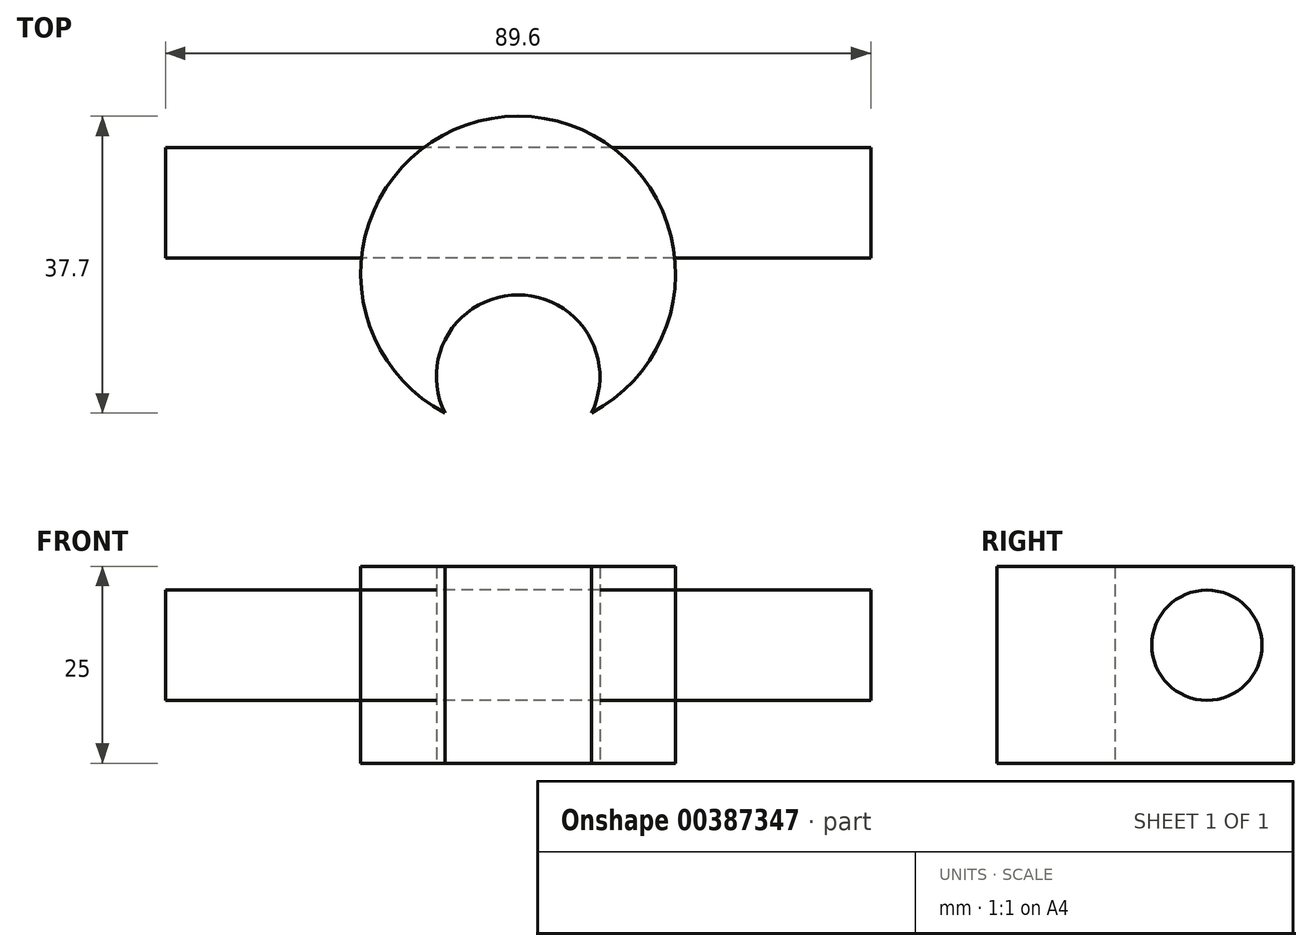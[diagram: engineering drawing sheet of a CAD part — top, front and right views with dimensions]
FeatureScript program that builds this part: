
annotation { "Feature Type Name" : "Feature", "Feature Type Description" : "" }
export const myFeature = defineFeature(function(context is Context, id is Id, definition is map)
    precondition{}
    {
        {
            var Q0;
            Q0=qCreatedBy(makeId("Top.planeOp"),FACE);
            var sketch = newSketch(context, id + "F0", { "sketchPlane" : qUnion([Q0])});
            skCircle(sketch, "E0", {"center": v(0, 0) * mm, "radius": 20 * mm});
            skCircle(sketch, "E1", {"center": v(0, -13.1) * mm, "radius": 10.39 * mm});
            skLineSegment(sketch, "E2", {"start": v(0, 20) * mm, "end": v(0, 20) * mm});
            skSolve(sketch);
        }
        {
            var Q0;
            {var subQ0=sQuery(id+"F0.wireOp",EDGE,"E1");var subQ1=sQuery(id+"F0.wireOp",EDGE,"E0");var subQ2=makeQuery(id+"F0.imprint","INTERSECT",VERTEX,{"disambiguationData":[OD(0.0)],"derivedFrom":[subQ1,subQ0]});Q0=makeQuery(id+"F0.imprint","IMPRINT",FACE,{"disambiguationData":[TD([[makeQuery(id+"F0.imprint","IMPRINT",EDGE,{"disambiguationData":[TD([[subQ2,1.0]])],"derivedFrom":subQ1}),1.0]])]});}
            extrude(context, id + "F1", {"entities" : qUnion([Q0]), "depth" : 25 * mm});
        }
        {
            var Q0;
            Q0=qCreatedBy(makeId("Right.planeOp"),FACE);
            var sketch = newSketch(context, id + "F2", { "sketchPlane" : qUnion([Q0])});
            skCircle(sketch, "E3", {"center": v(9, 15) * mm, "radius": 7 * mm});
            skSolve(sketch);
        }
        {
            var Q0;
            Q0=makeQuery(id+"F2.imprint","IMPRINT",FACE,{"disambiguationData":[TD([[makeQuery(id+"F2.imprint","IMPRINT",EDGE,{"derivedFrom":sQuery(id+"F2.wireOp",EDGE,"E3")}),1.0]])]});
            extrude(context, id + "F3", {"entities" : qUnion([Q0]), "endBound" : BoundingType.SYMMETRIC, "depth" : 89.6 * mm});
        }
    });
